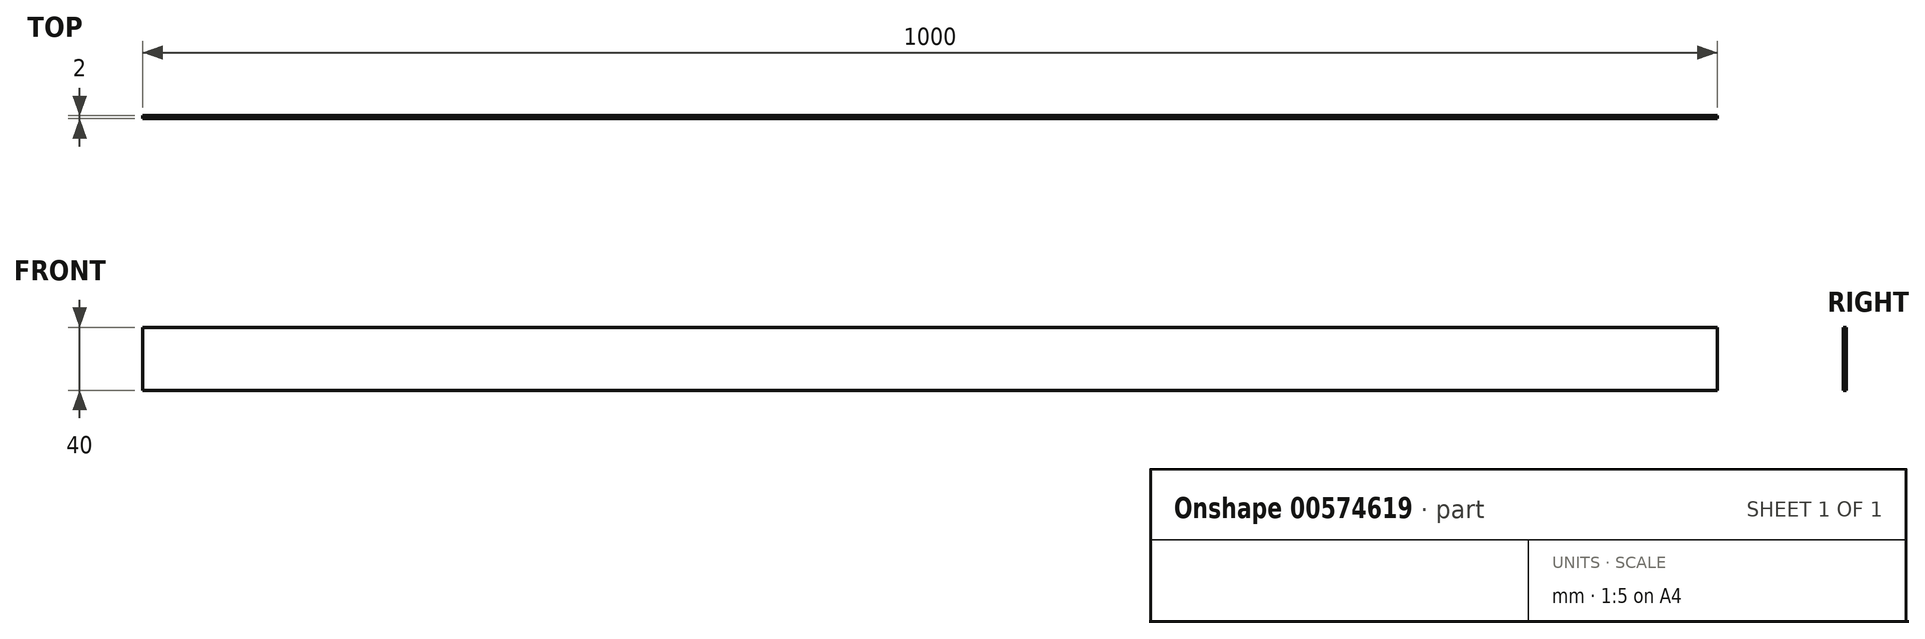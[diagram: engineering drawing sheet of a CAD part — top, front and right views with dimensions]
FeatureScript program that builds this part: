
annotation { "Feature Type Name" : "Feature", "Feature Type Description" : "" }
export const myFeature = defineFeature(function(context is Context, id is Id, definition is map)
    precondition{}
    {
        {
            var Q0;
            Q0=qCreatedBy(makeId("Front.planeOp"),FACE);
            var sketch = newSketch(context, id + "F0", { "sketchPlane" : qUnion([Q0])});
            skLineSegment(sketch, "E0.top", {"start": v(0, 40) * mm, "end": v(1000, 40) * mm});
            skLineSegment(sketch, "E0.left", {"start": v(0, 0) * mm, "end": v(0, 40) * mm});
            skLineSegment(sketch, "E0.right", {"start": v(1000, 0) * mm, "end": v(1000, 40) * mm});
            skLineSegment(sketch, "E1", {"start": v(0, 0) * mm, "end": v(1000, 0) * mm});
            skSolve(sketch);
        }
        {
            var Q0;
            Q0=makeQuery(id+"F0.imprint","IMPRINT",FACE,{"disambiguationData":[TD([[makeQuery(id+"F0.imprint","IMPRINT",EDGE,{"derivedFrom":sQuery(id+"F0.wireOp",EDGE,"E0.top")}),-1.0]])]});
            extrude(context, id + "F1", {"entities" : qUnion([Q0]), "depth" : 2 * mm, "offsetDistance" : 25 * mm});
        }
    });
